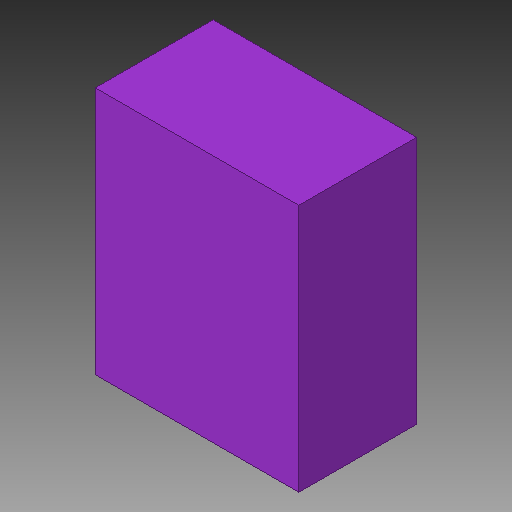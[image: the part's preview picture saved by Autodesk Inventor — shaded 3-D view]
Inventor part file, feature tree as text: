
AUTODESK INVENTOR PART (.ipt)
format: ipt  version: 2018 (Build 220112000, 112)  size: 81,920 bytes
history: native  units: in
note: dims shown in document units (in); Inventor stores cm internally (conversion verified against a paired STEP export)
features: other x1, extrude x1
ambient origin geometry x8: Origin, YZ Plane, XZ Plane, XY Plane, X Axis, Y Axis, Z Axis, Center Point
bodies: Solid1 (feature_tree)
feature tree (2):
  other  "DRY6, TPS62237DRY_173"
  extrude  "Extrusion1"  Depth=0.0394in TaperAngle=0.0deg
